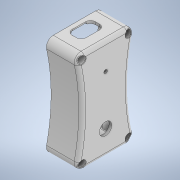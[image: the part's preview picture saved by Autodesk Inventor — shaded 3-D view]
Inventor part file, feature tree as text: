
AUTODESK INVENTOR PART (.ipt)
format: ipt  version: 2021 (Build 250183000, 183)  size: 608,256 bytes
history: native  units: mm
features: extrude x10, sketch x10, fillet x5, projected_geometry x4, mirror x2, shell x1, plane x1
ambient origin geometry x8: Origin, YZ Plane, XZ Plane, XY Plane, X Axis, Y Axis, Z Axis, Center Point
bodies: Solid1 (feature_tree)
feature tree (33):
  extrude  "Extrusion1"  Depth=27.0mm
  extrude  "Extrusion5"  Depth=2.0mm
  fillet  "Fillet1"  Radius=1.5mm
  shell  "Shell1"  Thickness=3.8mm
  extrude  "Extrusion6"  Depth=4.0mm
  extrude  "Extrusion7"  Depth=2.4mm
  fillet  "Fillet3"  Radius=17.78mm
  extrude  "Extrusion8"  Depth=6.8mm TaperAngle=0.0deg
  extrude  "Extrusion14"  Depth=11.4mm
  extrude  "Extrusion15"  Depth=13.5mm
  fillet  "Fillet8"  Radius=1.5mm
  extrude  "Extrusion16"  Depth=39.37mm
  fillet  "Fillet9"  Radius=7.1mm
  mirror  "Mirror5"
  plane  "Work Plane5"
  mirror  "Mirror8"
  extrude  "Extrusion17"  Depth=10.795mm
  extrude  "Extrusion18"  Depth=0.25mm
  fillet  "Fillet11"  Radius=5.5mm
  sketch  "Sketch1"  dims[d0=18.0mm d1=27.0mm]
  sketch  "Sketch5"  dims[d2=58.0mm d3=0.0mm d4=2.0mm d5=1.5mm d26=3.8mm]
  sketch  "Sketch6"  dims[d27=0.0mm d28=0.0mm d29=4.0mm]
  sketch  "Sketch7"  dims[d33=5.0mm d34=2.4mm d36=17.78mm]
  sketch  "Sketch8"  dims[d37=45.72mm d38=6.8mm d39=0.0mm]
  sketch  "Sketch18"  dims[d40=3.0mm d41=11.4mm]
  sketch  "Sketch19"  dims[d42=8.2mm d43=13.5mm d44=1.5mm d45=0.0mm]
  sketch  "Sketch20"  dims[d46=3.0mm d47=39.37mm d48=7.1mm]
  sketch  "Sketch21"  dims[d49=2.0mm d50=10.795mm]
  sketch  "Sketch22"  dims[d51=0.0mm d52=0.0mm d94=1.9mm d95=5.5mm d96=10.0mm d97=0.0mm d98=4.0mm d100=10.0mm d101=0.0mm d102=0.5mm d103=3.75mm d104=6.8mm d105=0.0mm d106=0.25mm d107=1.5mm d108=2.1mm d109=0.0mm d110=0.0mm d111=3.0mm d112=0.0mm d114=4.5mm d115=0.75mm d116=0.25mm]
  projected_geometry  "Project Cut Edges6"
  projected_geometry  "Project Cut Edges10"
  projected_geometry  "Project Cut Edges11"
  projected_geometry  "Project Cut Edges12"
